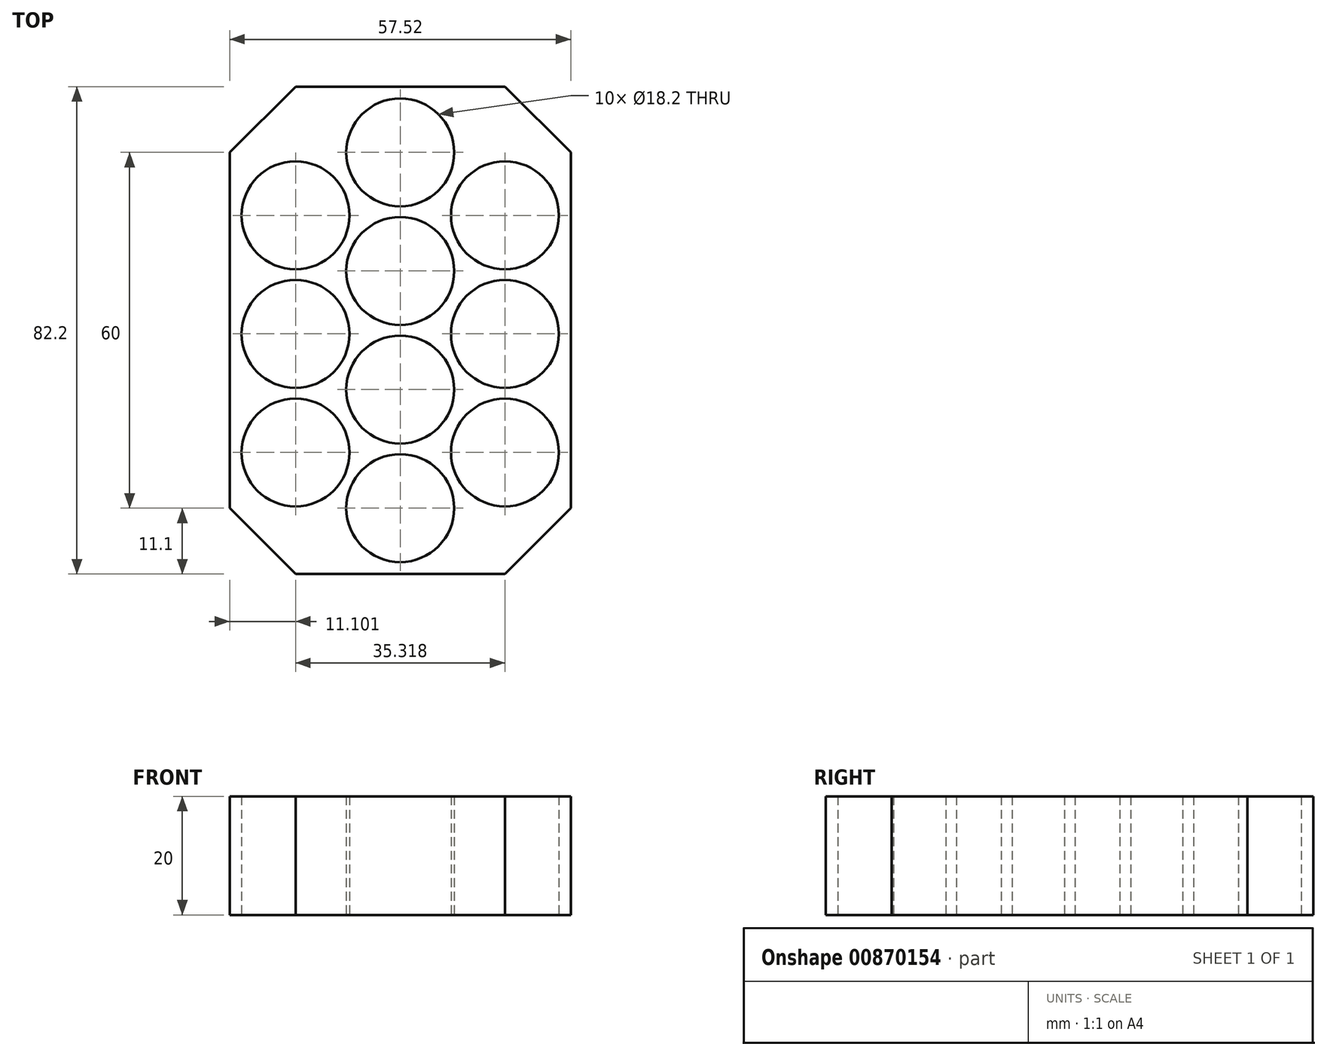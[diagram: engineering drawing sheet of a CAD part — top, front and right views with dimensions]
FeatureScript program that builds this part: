
annotation { "Feature Type Name" : "Feature", "Feature Type Description" : "" }
export const myFeature = defineFeature(function(context is Context, id is Id, definition is map)
    precondition{}
    {
        {
            var Q0;
            Q0=qCreatedBy(makeId("Top.planeOp"),FACE);
            var sketch = newSketch(context, id + "F0", { "sketchPlane" : qUnion([Q0])});
            skLineSegment(sketch, "E0", {"start": v(0, 0) * mm, "end": v(0, 20) * mm, "construction": true});
            skLineSegment(sketch, "E1", {"start": v(0, 20) * mm, "end": v(0, 40) * mm, "construction": true});
            skLineSegment(sketch, "E2", {"start": v(0, 0) * mm, "end": v(-17.66, 9.39) * mm, "construction": true});
            skLineSegment(sketch, "E3", {"start": v(0, 0) * mm, "end": v(17.66, 9.39) * mm, "construction": true});
            skLineSegment(sketch, "E4", {"start": v(0, 20) * mm, "end": v(-17.66, 29.39) * mm, "construction": true});
            skLineSegment(sketch, "E5", {"start": v(0, 20) * mm, "end": v(17.66, 29.39) * mm, "construction": true});
            skLineSegment(sketch, "E6", {"start": v(0, 40) * mm, "end": v(-17.66, 49.39) * mm, "construction": true});
            skLineSegment(sketch, "E7", {"start": v(0, 40) * mm, "end": v(17.66, 49.39) * mm, "construction": true});
            skCircle(sketch, "E8", {"center": v(-17.66, 49.39) * mm, "radius": 9.1 * mm});
            skCircle(sketch, "E9", {"center": v(-17.66, 29.39) * mm, "radius": 9.1 * mm});
            skCircle(sketch, "E10", {"center": v(-17.66, 9.39) * mm, "radius": 9.1 * mm});
            skCircle(sketch, "E11", {"center": v(17.66, 49.39) * mm, "radius": 9.1 * mm});
            skCircle(sketch, "E12", {"center": v(17.66, 29.39) * mm, "radius": 9.1 * mm});
            skCircle(sketch, "E13", {"center": v(17.66, 9.39) * mm, "radius": 9.1 * mm});
            skCircle(sketch, "E14", {"center": v(0, 40) * mm, "radius": 9.1 * mm});
            skCircle(sketch, "E15", {"center": v(0, 20) * mm, "radius": 9.1 * mm});
            skCircle(sketch, "E16", {"center": v(0, 0) * mm, "radius": 9.1 * mm});
            skLineSegment(sketch, "E17", {"start": v(0, 40) * mm, "end": v(0, 60) * mm, "construction": true});
            skCircle(sketch, "E18", {"center": v(0, 60) * mm, "radius": 9.1 * mm});
            skLineSegment(sketch, "E19", {"start": v(-28.76, 60) * mm, "end": v(-28.76, 0) * mm});
            skLineSegment(sketch, "E20", {"start": v(28.76, 60) * mm, "end": v(28.76, 0) * mm});
            skLineSegment(sketch, "E21", {"start": v(0, 0) * mm, "end": v(0, -9.1) * mm, "construction": true});
            skLineSegment(sketch, "E22", {"start": v(-17.66, 49.39) * mm, "end": v(-17.66, 9.39) * mm, "construction": true});
            skLineSegment(sketch, "E23", {"start": v(17.66, 49.39) * mm, "end": v(17.66, 9.39) * mm, "construction": true});
            skLineSegment(sketch, "E24", {"start": v(-17.66, 71.1) * mm, "end": v(17.66, 71.1) * mm});
            skLineSegment(sketch, "E25", {"start": v(17.66, 71.1) * mm, "end": v(28.76, 60) * mm});
            skLineSegment(sketch, "E26", {"start": v(-17.66, 71.1) * mm, "end": v(-28.76, 60) * mm});
            skLineSegment(sketch, "E27", {"start": v(-17.66, -11.1) * mm, "end": v(17.66, -11.1) * mm});
            skLineSegment(sketch, "E28", {"start": v(17.66, -11.1) * mm, "end": v(28.76, 0) * mm});
            skLineSegment(sketch, "E29", {"start": v(-17.66, -11.1) * mm, "end": v(-28.76, 0) * mm});
            skLineSegment(sketch, "E30", {"start": v(0, 20) * mm, "end": v(-17.66, 9.39) * mm, "construction": true});
            skLineSegment(sketch, "E31", {"start": v(0, 20) * mm, "end": v(17.66, 9.39) * mm, "construction": true});
            skLineSegment(sketch, "E32", {"start": v(0, 40) * mm, "end": v(-17.66, 29.39) * mm, "construction": true});
            skLineSegment(sketch, "E33", {"start": v(0, 40) * mm, "end": v(17.66, 29.39) * mm, "construction": true});
            skLineSegment(sketch, "E34", {"start": v(0, 60) * mm, "end": v(17.66, 49.39) * mm, "construction": true});
            skLineSegment(sketch, "E35", {"start": v(0, 60) * mm, "end": v(-17.66, 49.39) * mm, "construction": true});
            skSolve(sketch);
        }
        {
            var Q0;
            Q0 = qSketchRegion(id + "F0", true);
            extrude(context, id + "F1", {"entities" : qUnion([Q0]), "depth" : 20 * mm, "offsetDistance" : 25 * mm});
        }
    });
